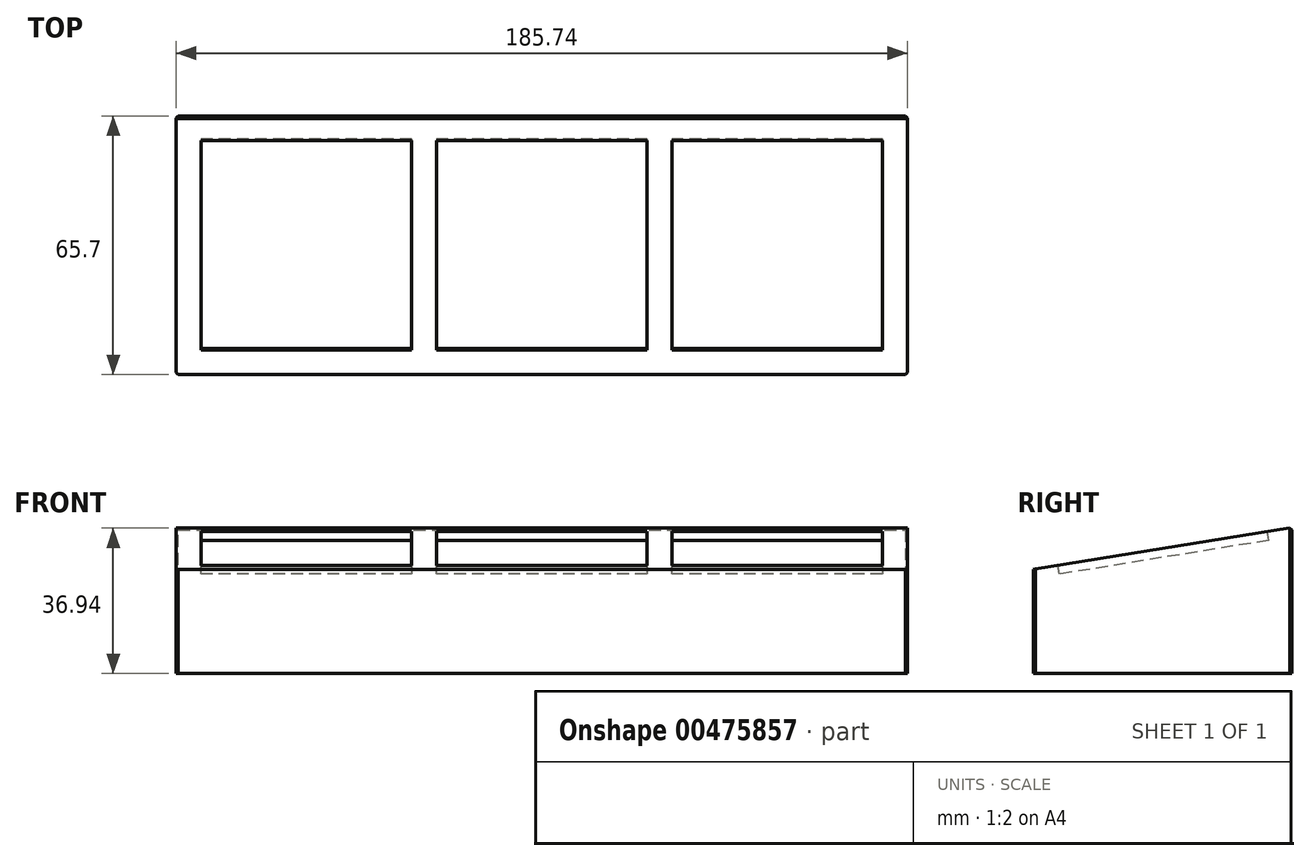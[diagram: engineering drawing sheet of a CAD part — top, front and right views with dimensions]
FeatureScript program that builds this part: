
annotation { "Feature Type Name" : "Feature", "Feature Type Description" : "" }
export const myFeature = defineFeature(function(context is Context, id is Id, definition is map)
    precondition{}
    {
        {
            var Q0;
            Q0=qCreatedBy(makeId("Top.planeOp"),FACE);
            var sketch = newSketch(context, id + "F0", { "sketchPlane" : qUnion([Q0])});
            skLineSegment(sketch, "E0.bottom", {"start": v(1114.42, -394.17) * mm, "end": v(-1114.42, -394.17) * mm});
            skLineSegment(sketch, "E0.top", {"start": v(1114.42, 394.17) * mm, "end": v(-1114.42, 394.17) * mm});
            skLineSegment(sketch, "E0.left", {"start": v(1114.42, -394.17) * mm, "end": v(1114.42, 394.17) * mm});
            skLineSegment(sketch, "E0.right", {"start": v(-1114.42, -394.17) * mm, "end": v(-1114.42, 394.17) * mm});
            skPoint(sketch, "E0.middle", {"position": v(0, 0) * mm});
            skSolve(sketch);
        }
        {
            var Q0;
            Q0=makeQuery(id+"F0.imprint","IMPRINT",FACE,{"disambiguationData":[TD([[makeQuery(id+"F0.imprint","IMPRINT",EDGE,{"derivedFrom":sQuery(id+"F0.wireOp",EDGE,"E0.bottom")}),-1.0]])]});
            extrude(context, id + "F1", {"entities" : qUnion([Q0]), "depth" : 444.5 * mm});
        }
        {
            var Q0;
            Q0=makeQuery(id+"F1.opExtrude","SWEPT_FACE",FACE,{"disambiguationData":[OSD([sQuery(id+"F0.wireOp",EDGE,"E0.right")])]});
            var sketch = newSketch(context, id + "F2", { "sketchPlane" : qUnion([Q0])});
            skLineSegment(sketch, "E1", {"start": v(394.17, 444.5) * mm, "end": v(394.17, 317.5) * mm});
            skLineSegment(sketch, "E2", {"start": v(394.17, 317.5) * mm, "end": v(-394.17, 444.5) * mm});
            skLineSegment(sketch, "E3", {"start": v(-394.17, 444.5) * mm, "end": v(394.17, 444.5) * mm});
            skSolve(sketch);
        }
        {
            var Q0;
            Q0=makeQuery(id+"F2.imprint","IMPRINT",FACE,{"disambiguationData":[TD([[makeQuery(id+"F2.imprint","IMPRINT",EDGE,{"derivedFrom":sQuery(id+"F2.wireOp",EDGE,"E1")}),-1.0]])]});
            extrude(context, id + "F3", {"entities" : qUnion([Q0]), "operationType" : NewBodyOperationType.REMOVE, "oppositeDirection" : true, "depth" : 2228.85 * mm});
        }
        {
            var Q0;
            Q0=makeQuery(id+"F3.boolean.opBoolean","COPY",FACE,{"derivedFrom":makeQuery(id+"F3.opExtrude","SWEPT_FACE",FACE,{"disambiguationData":[OSD([sQuery(id+"F2.wireOp",EDGE,"E2")])]})});
            var sketch = newSketch(context, id + "F4", { "sketchPlane" : qUnion([Q0])});
            skLineSegment(sketch, "E4", {"start": v(1114.42, -338.66) * mm, "end": v(1114.42, 459.85) * mm});
            skLineSegment(sketch, "E5", {"start": v(1114.43, 459.85) * mm, "end": v(-1114.43, 459.85) * mm});
            skLineSegment(sketch, "E6", {"start": v(-1114.42, 459.85) * mm, "end": v(-1114.42, -338.66) * mm});
            skLineSegment(sketch, "E7", {"start": v(-1114.43, -338.66) * mm, "end": v(1114.43, -338.66) * mm});
            skPoint(sketch, "E8.endSnap0", {"position": v(1114.42, 60.6) * mm});
            skPoint(sketch, "E9", {"position": v(-717.55, 60.6) * mm});
            skPoint(sketch, "E10", {"position": v(717.55, 60.6) * mm});
            skLineSegment(sketch, "E11", {"start": v(320.68, 60.6) * mm, "end": v(320.68, 383.65) * mm});
            skLineSegment(sketch, "E12", {"start": v(-396.87, 60.6) * mm, "end": v(-396.87, 383.65) * mm});
            skLineSegment(sketch, "E13", {"start": v(1038.23, 60.6) * mm, "end": v(1038.23, 383.65) * mm});
            skPoint(sketch, "E14.middle", {"position": v(0, 60.6) * mm});
            skLineSegment(sketch, "E15.bottom", {"start": v(1038.23, 383.65) * mm, "end": v(396.88, 383.65) * mm});
            skLineSegment(sketch, "E15.top", {"start": v(1038.23, -262.46) * mm, "end": v(396.88, -262.46) * mm});
            skLineSegment(sketch, "E15.left", {"start": v(1038.23, 383.65) * mm, "end": v(1038.23, -262.46) * mm});
            skLineSegment(sketch, "E15.right", {"start": v(396.88, 383.65) * mm, "end": v(396.88, -262.46) * mm});
            skLineSegment(sketch, "E16.bottom", {"start": v(320.68, 383.65) * mm, "end": v(-320.67, 383.65) * mm});
            skLineSegment(sketch, "E16.top", {"start": v(320.68, -262.46) * mm, "end": v(-320.67, -262.46) * mm});
            skLineSegment(sketch, "E16.left", {"start": v(320.68, 383.65) * mm, "end": v(320.68, -262.46) * mm});
            skLineSegment(sketch, "E16.right", {"start": v(-320.67, 383.65) * mm, "end": v(-320.67, -262.46) * mm});
            skLineSegment(sketch, "E17.bottom", {"start": v(-396.87, 383.65) * mm, "end": v(-1038.22, 383.65) * mm});
            skLineSegment(sketch, "E17.top", {"start": v(-396.87, -262.46) * mm, "end": v(-1038.22, -262.46) * mm});
            skLineSegment(sketch, "E17.left", {"start": v(-396.87, 383.65) * mm, "end": v(-396.87, -262.46) * mm});
            skLineSegment(sketch, "E17.right", {"start": v(-1038.22, 383.65) * mm, "end": v(-1038.22, -262.46) * mm});
            skSolve(sketch);
        }
        {
            var Q0;
            {var subQ3=sQuery(id+"F4.wireOp",EDGE,"E16.bottom");Q0=makeQuery(id+"F4.imprint","IMPRINT",FACE,{"disambiguationData":[TD([[makeQuery(id+"F4.imprint","IMPRINT",EDGE,{"derivedFrom":subQ3}),1.0]])]});}
            var Q1;
            {var subQ3=sQuery(id+"F4.wireOp",EDGE,"E17.bottom");Q1=makeQuery(id+"F4.imprint","IMPRINT",FACE,{"disambiguationData":[TD([[makeQuery(id+"F4.imprint","IMPRINT",EDGE,{"derivedFrom":subQ3}),1.0]])]});}
            var Q2;
            {var subQ3=sQuery(id+"F4.wireOp",EDGE,"E15.bottom");Q2=makeQuery(id+"F4.imprint","IMPRINT",FACE,{"disambiguationData":[TD([[makeQuery(id+"F4.imprint","IMPRINT",EDGE,{"derivedFrom":subQ3}),1.0]])]});}
            extrude(context, id + "F5", {"entities" : qUnion([Q0, Q1, Q2]), "operationType" : NewBodyOperationType.REMOVE, "oppositeDirection" : true, "depth" : 27.01 * mm});
        }
        {
            var Q0;
            Q0=makeQuery(id+"F5.boolean.opBoolean","COPY",EDGE,{"derivedFrom":makeQuery(id+"F5.opExtrude","CAP_EDGE",EDGE,{"disambiguationData":[OSD([sQuery(id+"F4.wireOp",EDGE,"E15.right")])],"isStart":true})});
            var Q1;
            Q1=makeQuery(id+"F5.boolean.opBoolean","COPY",EDGE,{"derivedFrom":makeQuery(id+"F5.opExtrude","CAP_EDGE",EDGE,{"disambiguationData":[OSD([sQuery(id+"F4.wireOp",EDGE,"E16.left")])],"isStart":true})});
            var Q2;
            Q2=makeQuery(id+"F5.boolean.opBoolean","COPY",EDGE,{"derivedFrom":makeQuery(id+"F5.opExtrude","CAP_EDGE",EDGE,{"disambiguationData":[OSD([sQuery(id+"F4.wireOp",EDGE,"E16.right")])],"isStart":true})});
            var Q3;
            Q3=makeQuery(id+"F5.boolean.opBoolean","COPY",EDGE,{"derivedFrom":makeQuery(id+"F5.opExtrude","CAP_EDGE",EDGE,{"disambiguationData":[OSD([sQuery(id+"F4.wireOp",EDGE,"E17.left")])],"isStart":true})});
            var Q4;
            Q4=makeQuery(id+"F5.boolean.opBoolean","COPY",EDGE,{"derivedFrom":makeQuery(id+"F5.opExtrude","CAP_EDGE",EDGE,{"disambiguationData":[OSD([sQuery(id+"F4.wireOp",EDGE,"E17.right")])],"isStart":true})});
            var Q5;
            Q5=makeQuery(id+"F5.boolean.opBoolean","COPY",EDGE,{"derivedFrom":makeQuery(id+"F5.opExtrude","CAP_EDGE",EDGE,{"disambiguationData":[OSD([sQuery(id+"F4.wireOp",EDGE,"E17.bottom")])],"isStart":true})});
            var Q6;
            Q6=makeQuery(id+"F5.boolean.opBoolean","COPY",EDGE,{"derivedFrom":makeQuery(id+"F5.opExtrude","CAP_EDGE",EDGE,{"disambiguationData":[OSD([sQuery(id+"F4.wireOp",EDGE,"E17.top")])],"isStart":true})});
            var Q7;
            Q7=makeQuery(id+"F5.boolean.opBoolean","COPY",EDGE,{"derivedFrom":makeQuery(id+"F5.opExtrude","CAP_EDGE",EDGE,{"disambiguationData":[OSD([sQuery(id+"F4.wireOp",EDGE,"E16.bottom")])],"isStart":true})});
            var Q8;
            Q8=makeQuery(id+"F5.boolean.opBoolean","COPY",EDGE,{"derivedFrom":makeQuery(id+"F5.opExtrude","CAP_EDGE",EDGE,{"disambiguationData":[OSD([sQuery(id+"F4.wireOp",EDGE,"E16.top")])],"isStart":true})});
            var Q9;
            Q9=makeQuery(id+"F5.boolean.opBoolean","COPY",EDGE,{"derivedFrom":makeQuery(id+"F5.opExtrude","CAP_EDGE",EDGE,{"disambiguationData":[OSD([sQuery(id+"F4.wireOp",EDGE,"E15.top")])],"isStart":true})});
            var Q10;
            Q10=makeQuery(id+"F5.boolean.opBoolean","COPY",EDGE,{"derivedFrom":makeQuery(id+"F5.opExtrude","CAP_EDGE",EDGE,{"disambiguationData":[OSD([sQuery(id+"F4.wireOp",EDGE,"E15.left")])],"isStart":true})});
            var Q11;
            Q11=makeQuery(id+"F5.boolean.opBoolean","COPY",EDGE,{"derivedFrom":makeQuery(id+"F5.opExtrude","CAP_EDGE",EDGE,{"disambiguationData":[OSD([sQuery(id+"F4.wireOp",EDGE,"E15.bottom")])],"isStart":true})});
            var Q12;
            {var subQ0=sQuery(id+"F0.wireOp",EDGE,"E0.top");Q12=makeQuery(id+"F3.boolean.opBoolean","MERGE",EDGE,{"derivedFrom":[makeQuery(id+"F1.opExtrude","CAP_EDGE",EDGE,{"disambiguationData":[OSD([subQ0])],"isStart":false}),makeQuery(id+"F3.opExtrude","SWEPT_EDGE",EDGE,{"disambiguationData":[OSD([subQ0,sQuery(id+"F0.wireOp",EDGE,"E0.right"),sQuery(id+"F2.wireOp",EDGE,"E2"),sQuery(id+"F2.wireOp",EDGE,"E3")])]})]});}
            var Q13;
            Q13=makeQuery(id+"F3.boolean.opBoolean","COPY",EDGE,{"derivedFrom":makeQuery(id+"F3.opExtrude","CAP_EDGE",EDGE,{"disambiguationData":[OSD([sQuery(id+"F2.wireOp",EDGE,"E2")])],"isStart":false})});
            var Q14;
            Q14=makeQuery(id+"F3.boolean.opBoolean","COPY",EDGE,{"derivedFrom":makeQuery(id+"F3.opExtrude","SWEPT_EDGE",EDGE,{"disambiguationData":[OSD([sQuery(id+"F0.wireOp",EDGE,"E0.bottom"),sQuery(id+"F0.wireOp",EDGE,"E0.right"),sQuery(id+"F2.wireOp",EDGE,"E1"),sQuery(id+"F2.wireOp",EDGE,"E2")])]})});
            var Q15;
            Q15=makeQuery(id+"F3.boolean.opBoolean","COPY",EDGE,{"derivedFrom":makeQuery(id+"F3.opExtrude","CAP_EDGE",EDGE,{"disambiguationData":[OSD([sQuery(id+"F2.wireOp",EDGE,"E2")])],"isStart":true})});
            var Q16;
            Q16=makeQuery(id+"F1.opExtrude","SWEPT_EDGE",EDGE,{"disambiguationData":[OSD([sQuery(id+"F0.wireOp",EDGE,"E0.top"),sQuery(id+"F0.wireOp",EDGE,"E0.right")])]});
            var Q17;
            Q17=makeQuery(id+"F1.opExtrude","SWEPT_EDGE",EDGE,{"disambiguationData":[OSD([sQuery(id+"F0.wireOp",EDGE,"E0.bottom"),sQuery(id+"F0.wireOp",EDGE,"E0.right")])]});
            var Q18;
            Q18=makeQuery(id+"F1.opExtrude","SWEPT_EDGE",EDGE,{"disambiguationData":[OSD([sQuery(id+"F0.wireOp",EDGE,"E0.bottom"),sQuery(id+"F0.wireOp",EDGE,"E0.left")])]});
            var Q19;
            Q19=makeQuery(id+"F1.opExtrude","SWEPT_EDGE",EDGE,{"disambiguationData":[OSD([sQuery(id+"F0.wireOp",EDGE,"E0.top"),sQuery(id+"F0.wireOp",EDGE,"E0.left")])]});
            chamfer(context, id + "F6", {"entities" : qUnion([Q0, Q1, Q2, Q3, Q4, Q5, Q6, Q7, Q8, Q9, Q10, Q11, Q12, Q13, Q14, Q15, Q16, Q17, Q18, Q19]), "width" : 6.35 * mm, "tangentPropagation" : true});
        }
        {
            var Q0;
            Q0=makeQuery(id+"F1.opExtrude","SWEPT_BODY",BODY,{"disambiguationData":[OSD([sQuery(id+"F0.wireOp",EDGE,"E0.bottom"),sQuery(id+"F0.wireOp",EDGE,"E0.top"),sQuery(id+"F0.wireOp",EDGE,"E0.left"),sQuery(id+"F0.wireOp",EDGE,"E0.right")])]});
            var Q1;
            Q1=qCreatedBy(makeId("Origin.pointOp"),VERTEX);
            transform(context, id + "F7", {"entities" : qUnion([Q0]), "transformType" : TransformType.SCALE_UNIFORMLY, "scale" : 1 / 12, "scalePoint" : qUnion([Q1]), "makeCopy" : false});
        }
    });
